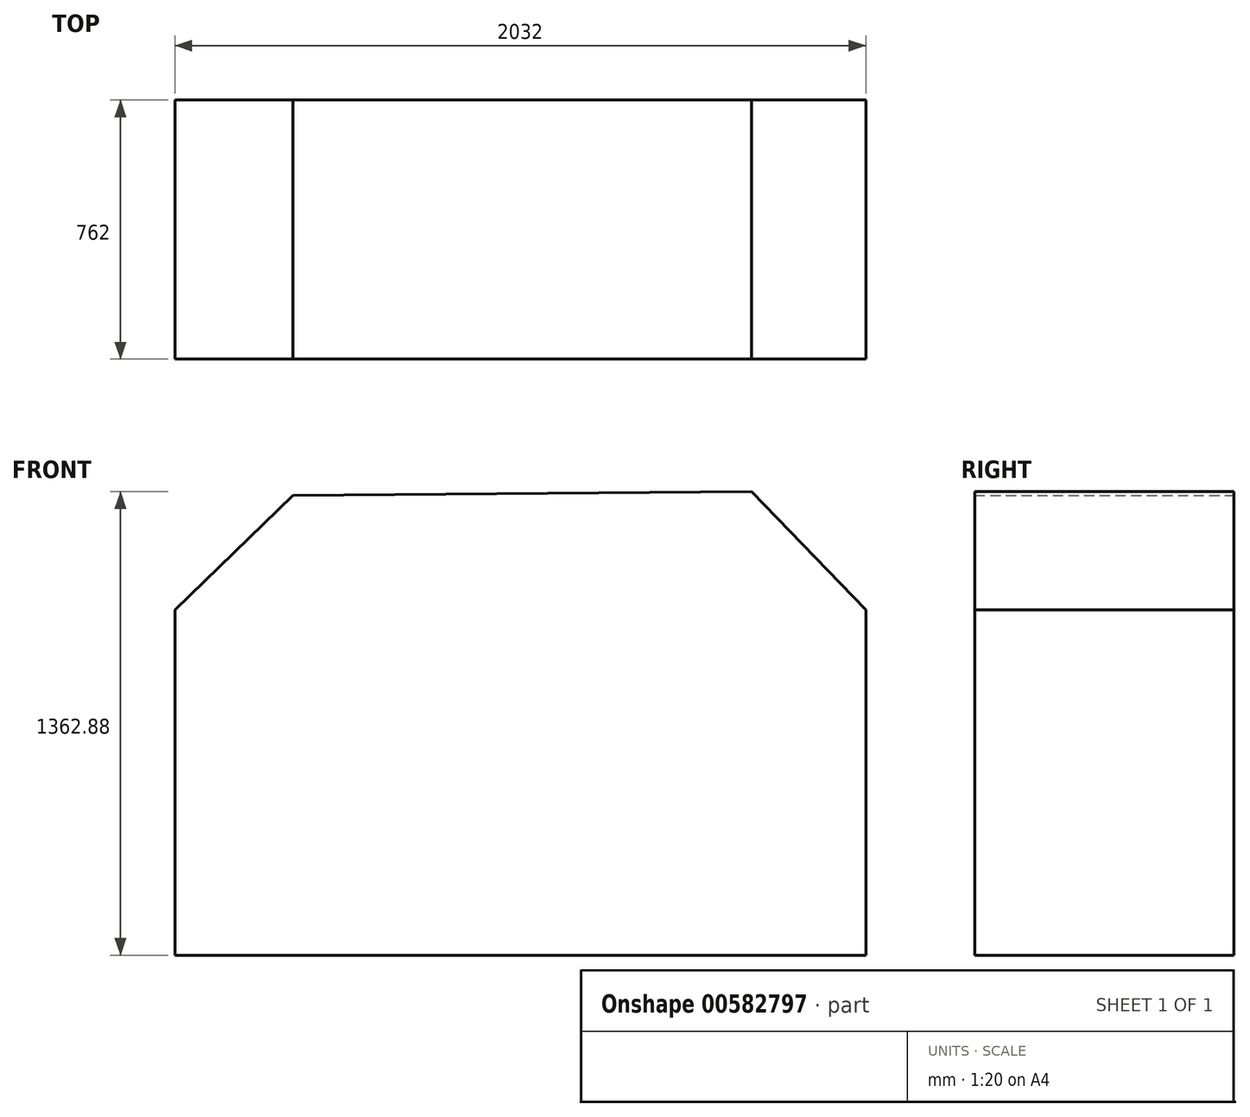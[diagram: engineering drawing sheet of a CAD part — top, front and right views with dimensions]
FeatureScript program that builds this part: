
annotation { "Feature Type Name" : "Feature", "Feature Type Description" : "" }
export const myFeature = defineFeature(function(context is Context, id is Id, definition is map)
    precondition{}
    {
        {
            var Q0;
            Q0=qCreatedBy(makeId("Front.planeOp"),FACE);
            var sketch = newSketch(context, id + "F0", { "sketchPlane" : qUnion([Q0])});
            skLineSegment(sketch, "E0", {"start": v(0, 0) * mm, "end": v(-1016, 0) * mm});
            skLineSegment(sketch, "E1", {"start": v(0, 0) * mm, "end": v(1016, 0) * mm});
            skLineSegment(sketch, "E2", {"start": v(-1016, 0) * mm, "end": v(-1016, 1016) * mm});
            skLineSegment(sketch, "E3", {"start": v(1016, 0) * mm, "end": v(1016, 1016) * mm});
            skLineSegment(sketch, "E4", {"start": v(-1016, 1016) * mm, "end": v(-669.12, 1351.52) * mm});
            skLineSegment(sketch, "E5", {"start": v(1016, 1016) * mm, "end": v(680.48, 1362.88) * mm});
            skLineSegment(sketch, "E6", {"start": v(-669.12, 1351.52) * mm, "end": v(680.48, 1362.88) * mm});
            skLineSegment(sketch, "E7", {"start": v(-1016, 1016) * mm, "end": v(1016, 1016) * mm});
            skLineSegment(sketch, "E8", {"start": v(-1016, 508) * mm, "end": v(1016, 508) * mm});
            skLineSegment(sketch, "E9.bottom", {"start": v(-1016, 0) * mm, "end": v(1016, 0) * mm});
            skLineSegment(sketch, "E9.top", {"start": v(-1016, -76.2) * mm, "end": v(1016, -76.2) * mm});
            skLineSegment(sketch, "E9.left", {"start": v(-1016, 0) * mm, "end": v(-1016, -76.2) * mm});
            skLineSegment(sketch, "E9.right", {"start": v(1016, 0) * mm, "end": v(1016, -76.2) * mm});
            skSolve(sketch);
        }
        {
            var Q0;
            Q0=makeQuery(id+"F0.imprint","IMPRINT",FACE,{"disambiguationData":[TD([[makeQuery(id+"F0.imprint","IMPRINT",EDGE,{"derivedFrom":sQuery(id+"F0.wireOp",EDGE,"E4")}),-1.0]])]});
            var Q1;
            {var subQ0=sQuery(id+"F0.wireOp",EDGE,"E7");Q1=makeQuery(id+"F0.imprint","IMPRINT",FACE,{"disambiguationData":[TD([[makeQuery(id+"F0.imprint","IMPRINT",EDGE,{"derivedFrom":subQ0}),-1.0]])]});}
            var Q2;
            {var subQ2=sQuery(id+"F0.wireOp",EDGE,"E8");Q2=makeQuery(id+"F0.imprint","IMPRINT",FACE,{"disambiguationData":[TD([[makeQuery(id+"F0.imprint","IMPRINT",EDGE,{"derivedFrom":subQ2}),-1.0]])]});}
            var Q3;
            Q3=makeQuery(id+"F0.imprint","IMPRINT",FACE,{"disambiguationData":[TD([[makeQuery(id+"F0.imprint","IMPRINT",EDGE,{"derivedFrom":sQuery(id+"F0.wireOp",EDGE,"E9.bottom")}),-1.0]])]});
            extrude(context, id + "F1", {"entities" : qUnion([Q0, Q1, Q2, Q3]), "depth" : 762 * mm, "offsetDistance" : 25.4 * mm});
        }
        {
            var Q0;
            Q0=makeQuery(id+"F1.opExtrude","SWEPT_FACE",FACE,{"disambiguationData":[OSD([sQuery(id+"F0.wireOp",EDGE,"E2")])]});
            var sketch = newSketch(context, id + "F2", { "sketchPlane" : qUnion([Q0])});
            skLineSegment(sketch, "E10.bottom", {"start": v(76.2, 1016) * mm, "end": v(711.2, 1016) * mm});
            skLineSegment(sketch, "E10.top", {"start": v(76.2, 685.8) * mm, "end": v(711.2, 685.8) * mm});
            skLineSegment(sketch, "E10.left", {"start": v(76.2, 685.8) * mm, "end": v(76.2, 1016) * mm});
            skLineSegment(sketch, "E10.right", {"start": v(711.2, 685.8) * mm, "end": v(711.2, 1016) * mm});
            skLineSegment(sketch, "E11.bottom", {"start": v(106.08, -29.76) * mm, "end": v(697.34, -29.76) * mm});
            skLineSegment(sketch, "E11.top", {"start": v(106.08, 504.47) * mm, "end": v(697.34, 504.47) * mm});
            skLineSegment(sketch, "E11.left", {"start": v(106.08, -29.76) * mm, "end": v(106.08, 504.47) * mm});
            skLineSegment(sketch, "E11.right", {"start": v(697.34, -29.76) * mm, "end": v(697.34, 504.47) * mm});
            skSolve(sketch);
        }
        {
            var Q0;
            Q0=makeQuery(id+"F2.imprint","IMPRINT",FACE,{"disambiguationData":[TD([[makeQuery(id+"F2.imprint","IMPRINT",EDGE,{"derivedFrom":sQuery(id+"F2.wireOp",EDGE,"E10.bottom")}),-1.0]])]});
            var Q1;
            Q1=makeQuery(id+"F2.imprint","IMPRINT",FACE,{"disambiguationData":[TD([[makeQuery(id+"F2.imprint","IMPRINT",EDGE,{"derivedFrom":sQuery(id+"F2.wireOp",EDGE,"E11.bottom")}),1.0]])]});
            extrude(context, id + "F3", {"entities" : qUnion([Q0, Q1]), "operationType" : NewBodyOperationType.REMOVE, "oppositeDirection" : true, "depth" : 2032 * mm, "offsetDistance" : 25.4 * mm});
        }
    });
